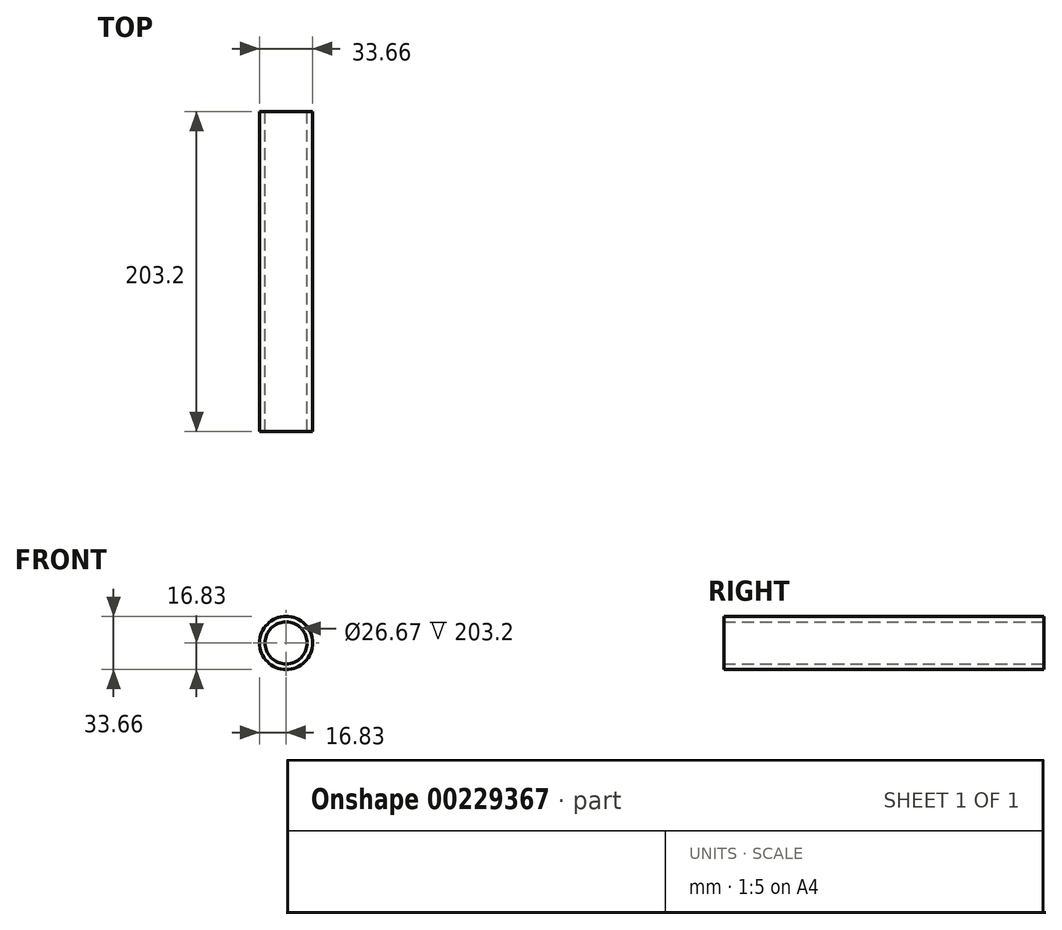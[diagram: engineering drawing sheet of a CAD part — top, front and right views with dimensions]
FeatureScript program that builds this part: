
annotation { "Feature Type Name" : "Feature", "Feature Type Description" : "" }
export const myFeature = defineFeature(function(context is Context, id is Id, definition is map)
    precondition{}
    {
        {
            var Q0;
            Q0=qCreatedBy(makeId("Front.planeOp"),FACE);
            var sketch = newSketch(context, id + "F0", { "sketchPlane" : qUnion([Q0])});
            skCircle(sketch, "E0", {"center": v(0, 0) * mm, "radius": 13.34 * mm});
            skCircle(sketch, "E1", {"center": v(0, 0) * mm, "radius": 16.83 * mm});
            skSolve(sketch);
        }
        {
            var Q0;
            Q0=makeQuery(id+"F0.imprint","IMPRINT",FACE,{"disambiguationData":[TD([[makeQuery(id+"F0.imprint","IMPRINT",EDGE,{"derivedFrom":sQuery(id+"F0.wireOp",EDGE,"E0")}),-1.0]])]});
            extrude(context, id + "F1", {"entities" : qUnion([Q0]), "depth" : 203.2 * mm});
        }
    });
